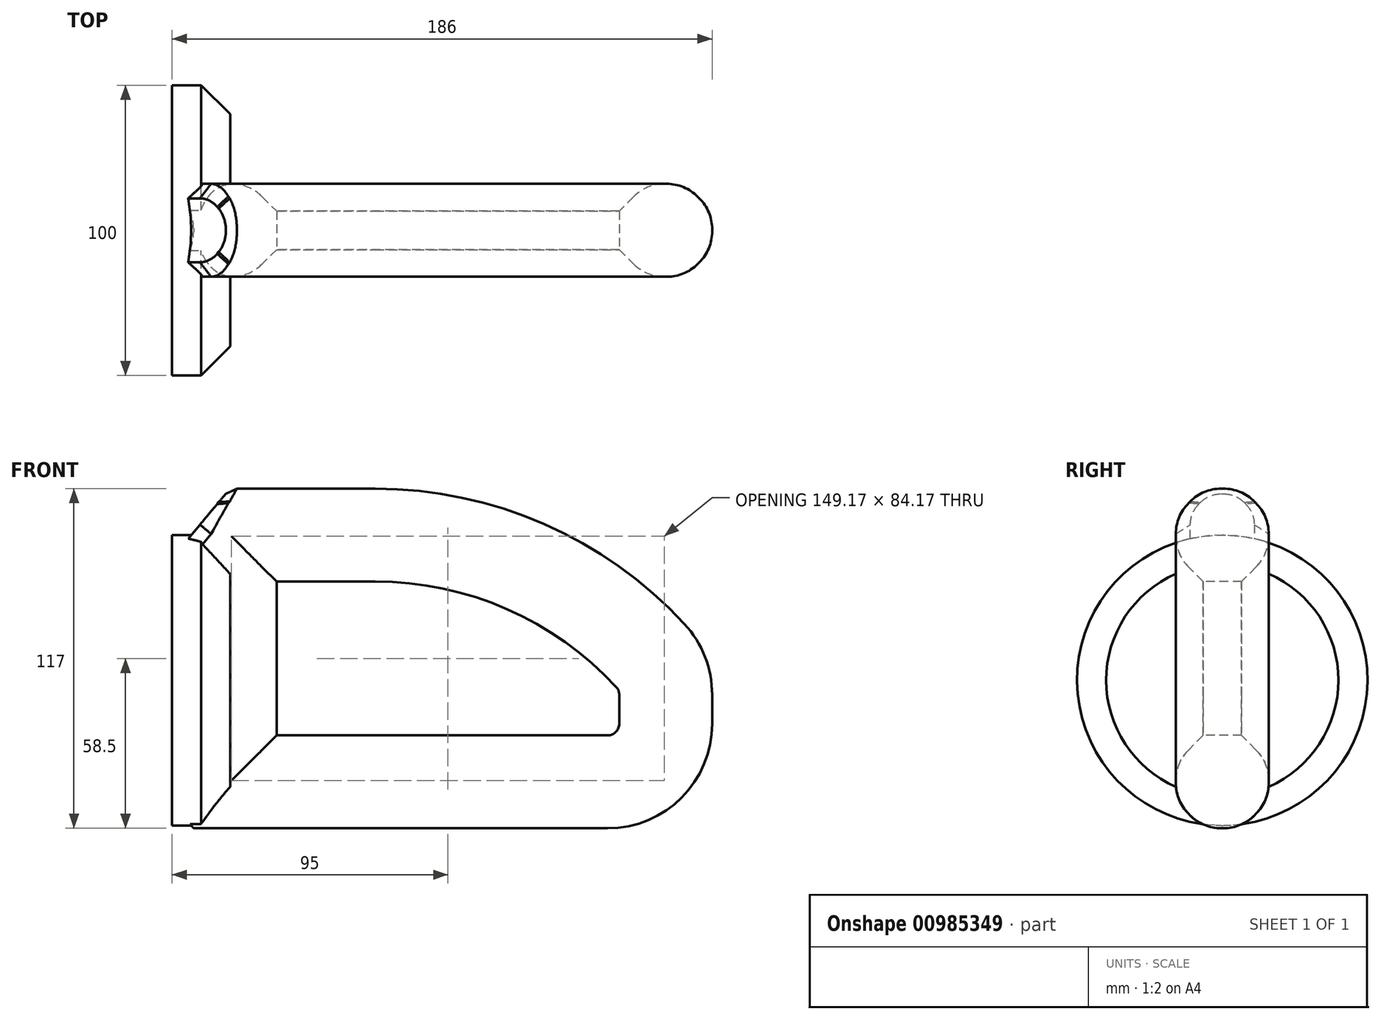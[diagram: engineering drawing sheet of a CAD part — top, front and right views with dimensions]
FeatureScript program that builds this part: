
annotation { "Feature Type Name" : "Feature", "Feature Type Description" : "" }
export const myFeature = defineFeature(function(context is Context, id is Id, definition is map)
    precondition{}
    {
        {
            var Q0;
            Q0=qCreatedBy(makeId("Front.planeOp"),FACE);
            var sketch = newSketch(context, id + "F0", { "sketchPlane" : qUnion([Q0])});
            skLineSegment(sketch, "E0", {"start": v(0, 50) * mm, "end": v(0, -35) * mm});
            skLineSegment(sketch, "E1", {"start": v(0, -35) * mm, "end": v(130, -35) * mm});
            skLineSegment(sketch, "E2", {"start": v(150, -15) * mm, "end": v(150, -5) * mm});
            skLineSegment(sketch, "E3", {"start": v(50, 50) * mm, "end": v(0, 50) * mm});
            skArc(sketch, "E4.filletArc", {"start": v(144.69, 8.57) * mm, "mid": v(101.68, 39.2) * mm, "end": v(50, 50) * mm});
            skArc(sketch, "E5.filletArc", {"start": v(130, -35) * mm, "mid": v(144.14, -29.14) * mm, "end": v(150, -15) * mm});
            skArc(sketch, "E6.filletArc", {"start": v(150, -5) * mm, "mid": v(148.62, 2.29) * mm, "end": v(144.69, 8.57) * mm});
            skSolve(sketch);
        }
        {
            var Q0;
            Q0=qCreatedBy(makeId("Right.planeOp"),FACE);
            var sketch = newSketch(context, id + "F1", { "sketchPlane" : qUnion([Q0])});
            skCircle(sketch, "E7.cCircle", {"center": v(0, 50) * mm, "radius": 16 * mm, "construction": true});
            skLineSegment(sketch, "E7.0", {"start": v(-6.63, 34) * mm, "end": v(-16, 43.37) * mm});
            skLineSegment(sketch, "E7.1", {"start": v(-16, 43.37) * mm, "end": v(-16, 56.63) * mm});
            skLineSegment(sketch, "E7.2", {"start": v(-16, 56.63) * mm, "end": v(-6.63, 66) * mm});
            skLineSegment(sketch, "E7.3", {"start": v(-6.63, 66) * mm, "end": v(6.63, 66) * mm});
            skLineSegment(sketch, "E7.4", {"start": v(6.63, 66) * mm, "end": v(16, 56.63) * mm});
            skLineSegment(sketch, "E7.5", {"start": v(16, 56.63) * mm, "end": v(16, 43.37) * mm});
            skLineSegment(sketch, "E7.6", {"start": v(16, 43.37) * mm, "end": v(6.63, 34) * mm});
            skLineSegment(sketch, "E7.7", {"start": v(6.63, 34) * mm, "end": v(-6.63, 34) * mm});
            skPoint(sketch, "E7.0.midPoint", {"position": v(-11.31, 38.69) * mm});
            skSolve(sketch);
        }
        {
            var Q0;
            Q0=qSketchRegion(id+"F1",true);
            var Q1;
            Q1=qConstructionFilter(qBodyType(qCreatedBy(id+"F0",EDGE),BodyType.WIRE),ConstructionObject.NO);
            sweep(context, id + "F2", {"profiles" : qUnion([Q0]), "path" : qUnion([Q1])});
        }
        {
            var Q0;
            Q0=makeQuery(id+"F2.opSweep","SWEPT_FACE",FACE,{"disambiguationData":[OSD([sQuery(id+"F0.wireOp",EDGE,"E1"),sQuery(id+"F1.wireOp",EDGE,"E7.3")])]});
            var Q1;
            Q1=makeQuery(id+"F2.opSweep","SWEPT_FACE",FACE,{"disambiguationData":[OSD([sQuery(id+"F0.wireOp",EDGE,"E3"),sQuery(id+"F1.wireOp",EDGE,"E7.3")])]});
            var Q2;
            Q2=makeQuery(id+"F2.opSweep","SWEPT_FACE",FACE,{"disambiguationData":[OSD([sQuery(id+"F0.wireOp",EDGE,"E4.filletArc"),sQuery(id+"F1.wireOp",EDGE,"E7.3")])]});
            var Q3;
            Q3=makeQuery(id+"F2.opSweep","SWEPT_FACE",FACE,{"disambiguationData":[OSD([sQuery(id+"F0.wireOp",EDGE,"E6.filletArc"),sQuery(id+"F1.wireOp",EDGE,"E7.3")])]});
            var Q4;
            Q4=makeQuery(id+"F2.opSweep","SWEPT_FACE",FACE,{"disambiguationData":[OSD([sQuery(id+"F0.wireOp",EDGE,"E2"),sQuery(id+"F1.wireOp",EDGE,"E7.3")])]});
            var Q5;
            Q5=makeQuery(id+"F2.opSweep","SWEPT_FACE",FACE,{"disambiguationData":[OSD([sQuery(id+"F0.wireOp",EDGE,"E5.filletArc"),sQuery(id+"F1.wireOp",EDGE,"E7.3")])]});
            var Q6;
            Q6=makeQuery(id+"F2.opSweep","SWEPT_FACE",FACE,{"disambiguationData":[OSD([sQuery(id+"F0.wireOp",EDGE,"E3"),sQuery(id+"F1.wireOp",EDGE,"E7.5")])]});
            var Q7;
            Q7=makeQuery(id+"F2.opSweep","SWEPT_FACE",FACE,{"disambiguationData":[OSD([sQuery(id+"F0.wireOp",EDGE,"E3"),sQuery(id+"F1.wireOp",EDGE,"E7.1")])]});
            fillet(context, id + "F3", {"entities" : qUnion([Q0, Q1, Q2, Q3, Q4, Q5, Q6, Q7]), "radius" : 15 * mm, "tangentPropagation" : true, "allowEdgeOverflow" : false});
        }
        {
            var Q0;
            Q0=qCreatedBy(makeId("Right.planeOp"),FACE);
            var sketch = newSketch(context, id + "F4", { "sketchPlane" : qUnion([Q0])});
            skArc(sketch, "E8.0", {"start": v(16, 50.41) * mm, "mid": v(14.86, 56.15) * mm, "end": v(11.6, 61.02) * mm});
            skLineSegment(sketch, "E8.1", {"start": v(11.02, 61.6) * mm, "end": v(11.6, 61.02) * mm});
            skArc(sketch, "E8.2", {"start": v(0.41, 66) * mm, "mid": v(6.15, 64.86) * mm, "end": v(11.02, 61.6) * mm});
            skLineSegment(sketch, "E8.3", {"start": v(0.41, 66) * mm, "end": v(-0.41, 66) * mm});
            skArc(sketch, "E8.4", {"start": v(-11.02, 61.6) * mm, "mid": v(-6.15, 64.86) * mm, "end": v(-0.41, 66) * mm});
            skLineSegment(sketch, "E8.5", {"start": v(-11.6, 61.02) * mm, "end": v(-11.02, 61.6) * mm});
            skArc(sketch, "E8.6", {"start": v(-11.6, 61.02) * mm, "mid": v(-14.86, 56.15) * mm, "end": v(-16, 50.41) * mm});
            skLineSegment(sketch, "E8.7", {"start": v(16, -35.41) * mm, "end": v(16, 50.41) * mm});
            skLineSegment(sketch, "E8.8", {"start": v(-16, 50.41) * mm, "end": v(-16, -35.41) * mm});
            skArc(sketch, "E9.0", {"start": v(16, -35.41) * mm, "mid": v(14.86, -41.15) * mm, "end": v(11.6, -46.02) * mm});
            skLineSegment(sketch, "E9.1", {"start": v(11.02, -46.6) * mm, "end": v(11.6, -46.02) * mm});
            skArc(sketch, "E9.2", {"start": v(0.41, -51) * mm, "mid": v(6.15, -49.86) * mm, "end": v(11.02, -46.6) * mm});
            skLineSegment(sketch, "E9.3", {"start": v(-0.41, -51) * mm, "end": v(0.41, -51) * mm});
            skArc(sketch, "E9.4", {"start": v(-11.02, -46.6) * mm, "mid": v(-6.15, -49.86) * mm, "end": v(-0.41, -51) * mm});
            skLineSegment(sketch, "E9.5", {"start": v(-11.6, -46.02) * mm, "end": v(-11.02, -46.6) * mm});
            skArc(sketch, "E9.6", {"start": v(-11.6, -46.02) * mm, "mid": v(-14.86, -41.15) * mm, "end": v(-16, -35.41) * mm});
            skSolve(sketch);
        }
        {
            var Q0;
            Q0=qSketchRegion(id+"F4",true);
            var Q1;
            Q1=makeQuery(id+"F2.opSweep","SWEPT_FACE",FACE,{"disambiguationData":[OSD([sQuery(id+"F0.wireOp",EDGE,"E0"),sQuery(id+"F1.wireOp",EDGE,"E7.3")])]});
            extrude(context, id + "F5", {"entities" : qUnion([Q0]), "operationType" : NewBodyOperationType.ADD, "endBound" : BoundingType.UP_TO_SURFACE, "oppositeDirection" : true, "endBoundEntityFace" : qUnion([Q1]), "depth" : 25 * mm});
        }
        {
            var Q0;
            Q0=qCreatedBy(makeId("Front.planeOp"),FACE);
            var sketch = newSketch(context, id + "F6", { "sketchPlane" : qUnion([Q0])});
            skLineSegment(sketch, "E10", {"start": v(0, 66) * mm, "end": v(-16, 46.93) * mm});
            skLineSegment(sketch, "E11", {"start": v(-16, 46.93) * mm, "end": v(-16, 66) * mm});
            skLineSegment(sketch, "E12", {"start": v(-16, 66) * mm, "end": v(0, 66) * mm});
            skLineSegment(sketch, "E13.MirrorCS", {"start": v(-16, -46.93) * mm, "end": v(-16, -66) * mm});
            skLineSegment(sketch, "E14.MirrorCS", {"start": v(-16, -66) * mm, "end": v(0, -66) * mm});
            skLineSegment(sketch, "E15.MirrorCS", {"start": v(0, -66) * mm, "end": v(-16, -46.93) * mm});
            skSolve(sketch);
        }
        {
            var Q0;
            Q0=qSketchRegion(id+"F6",true);
            extrude(context, id + "F7", {"entities" : qUnion([Q0]), "operationType" : NewBodyOperationType.REMOVE, "endBound" : BoundingType.THROUGH_ALL, "oppositeDirection" : true, "depth" : 25 * mm, "hasSecondDirection" : true, "secondDirectionBound" : SecondDirectionBoundingType.THROUGH_ALL, "secondDirectionOppositeDirection" : false, "secondDirectionDepth" : 25 * mm});
        }
        {
            var Q0;
            Q0=qCreatedBy(makeId("Right.planeOp"),FACE);
            var sketch = newSketch(context, id + "F8", { "sketchPlane" : qUnion([Q0])});
            skCircle(sketch, "E16", {"center": v(0, 0) * mm, "radius": 50 * mm});
            skSolve(sketch);
        }
        {
            var Q0;
            Q0=qSketchRegion(id+"F8",true);
            extrude(context, id + "F9", {"entities" : qUnion([Q0]), "operationType" : NewBodyOperationType.ADD, "oppositeDirection" : true, "depth" : 20 * mm});
        }
        {
            var Q0;
            {var subQ0=sQuery(id+"F8.wireOp",EDGE,"E16");Q0=makeQuery(id+"F9.boolean.opBoolean","SPLIT",EDGE,{"disambiguationData":[TD([makeQuery(id+"F5.opExtrude","SWEPT_FACE",FACE,{"disambiguationData":[OSD([sQuery(id+"F4.wireOp",EDGE,"E8.8")])]})])],"derivedFrom":makeQuery(id+"F9.opExtrude","CAP_EDGE",EDGE,{"disambiguationData":[OSD([subQ0])],"isStart":true})});}
            var Q1;
            {var subQ0=sQuery(id+"F8.wireOp",EDGE,"E16");Q1=makeQuery(id+"F9.boolean.opBoolean","SPLIT",EDGE,{"disambiguationData":[TD([makeQuery(id+"F5.opExtrude","SWEPT_FACE",FACE,{"disambiguationData":[OSD([sQuery(id+"F4.wireOp",EDGE,"E8.7")])]})])],"derivedFrom":makeQuery(id+"F9.opExtrude","CAP_EDGE",EDGE,{"disambiguationData":[OSD([subQ0])],"isStart":true})});}
            chamfer(context, id + "F10", {"entities" : qUnion([Q0, Q1]), "width" : 10 * mm, "tangentPropagation" : true});
        }
        {
            var Q0;
            Q0=makeQuery(id+"F7.boolean.opBoolean","INTERSECT",EDGE,{"derivedFrom":[makeQuery(id+"F5.boolean.opBoolean","MERGE",FACE,{"derivedFrom":[makeQuery(id+"F2.opSweep","SWEPT_FACE",FACE,{"disambiguationData":[OSD([sQuery(id+"F0.wireOp",EDGE,"E3"),sQuery(id+"F1.wireOp",EDGE,"E7.1")])]}),makeQuery(id+"F5.opExtrude","SWEPT_FACE",FACE,{"disambiguationData":[OSD([sQuery(id+"F4.wireOp",EDGE,"E8.8")])]})]}),makeQuery(id+"F7.opExtrude","SWEPT_FACE",FACE,{"disambiguationData":[OSD([sQuery(id+"F6.wireOp",EDGE,"E10")])]})]});
            var Q1;
            Q1=makeQuery(id+"F7.boolean.opBoolean","INTERSECT",EDGE,{"derivedFrom":[makeQuery(id+"F5.boolean.opBoolean","MERGE",FACE,{"derivedFrom":[makeQuery(id+"F3.opFillet","BLEND_FACE",FACE,{"disambiguationData":[OSD([sQuery(id+"F0.wireOp",EDGE,"E3"),sQuery(id+"F1.wireOp",EDGE,"E7.1"),sQuery(id+"F1.wireOp",EDGE,"E7.2")])]}),makeQuery(id+"F5.opExtrude","SWEPT_FACE",FACE,{"disambiguationData":[OSD([sQuery(id+"F4.wireOp",EDGE,"E8.6")])]})]}),makeQuery(id+"F7.opExtrude","SWEPT_FACE",FACE,{"disambiguationData":[OSD([sQuery(id+"F6.wireOp",EDGE,"E10")])]})]});
            var Q2;
            Q2=makeQuery(id+"F7.boolean.opBoolean","INTERSECT",EDGE,{"derivedFrom":[makeQuery(id+"F5.boolean.opBoolean","MERGE",FACE,{"derivedFrom":[makeQuery(id+"F2.opSweep","SWEPT_FACE",FACE,{"disambiguationData":[OSD([sQuery(id+"F0.wireOp",EDGE,"E3"),sQuery(id+"F1.wireOp",EDGE,"E7.2")])]}),makeQuery(id+"F5.opExtrude","SWEPT_FACE",FACE,{"disambiguationData":[OSD([sQuery(id+"F4.wireOp",EDGE,"E8.5")])]})]}),makeQuery(id+"F7.opExtrude","SWEPT_FACE",FACE,{"disambiguationData":[OSD([sQuery(id+"F6.wireOp",EDGE,"E10")])]})]});
            var Q3;
            Q3=makeQuery(id+"F7.boolean.opBoolean","INTERSECT",EDGE,{"derivedFrom":[makeQuery(id+"F5.boolean.opBoolean","MERGE",FACE,{"derivedFrom":[makeQuery(id+"F3.opFillet","BLEND_FACE",FACE,{"disambiguationData":[OSD([sQuery(id+"F0.wireOp",EDGE,"E3"),sQuery(id+"F1.wireOp",EDGE,"E7.2"),sQuery(id+"F1.wireOp",EDGE,"E7.3")])]}),makeQuery(id+"F5.opExtrude","SWEPT_FACE",FACE,{"disambiguationData":[OSD([sQuery(id+"F4.wireOp",EDGE,"E8.4")])]})]}),makeQuery(id+"F7.opExtrude","SWEPT_FACE",FACE,{"disambiguationData":[OSD([sQuery(id+"F6.wireOp",EDGE,"E10")])]})]});
            var Q4;
            Q4=makeQuery(id+"F7.boolean.opBoolean","INTERSECT",EDGE,{"derivedFrom":[makeQuery(id+"F5.boolean.opBoolean","MERGE",FACE,{"derivedFrom":[makeQuery(id+"F2.opSweep","SWEPT_FACE",FACE,{"disambiguationData":[OSD([sQuery(id+"F0.wireOp",EDGE,"E3"),sQuery(id+"F1.wireOp",EDGE,"E7.5")])]}),makeQuery(id+"F5.opExtrude","SWEPT_FACE",FACE,{"disambiguationData":[OSD([sQuery(id+"F4.wireOp",EDGE,"E8.7")])]})]}),makeQuery(id+"F7.opExtrude","SWEPT_FACE",FACE,{"disambiguationData":[OSD([sQuery(id+"F6.wireOp",EDGE,"E10")])]})]});
            var Q5;
            Q5=makeQuery(id+"F7.boolean.opBoolean","INTERSECT",EDGE,{"derivedFrom":[makeQuery(id+"F5.boolean.opBoolean","MERGE",FACE,{"derivedFrom":[makeQuery(id+"F3.opFillet","BLEND_FACE",FACE,{"disambiguationData":[OSD([sQuery(id+"F0.wireOp",EDGE,"E3"),sQuery(id+"F1.wireOp",EDGE,"E7.4"),sQuery(id+"F1.wireOp",EDGE,"E7.5")])]}),makeQuery(id+"F5.opExtrude","SWEPT_FACE",FACE,{"disambiguationData":[OSD([sQuery(id+"F4.wireOp",EDGE,"E8.0")])]})]}),makeQuery(id+"F7.opExtrude","SWEPT_FACE",FACE,{"disambiguationData":[OSD([sQuery(id+"F6.wireOp",EDGE,"E10")])]})]});
            var Q6;
            Q6=makeQuery(id+"F7.boolean.opBoolean","INTERSECT",EDGE,{"derivedFrom":[makeQuery(id+"F5.boolean.opBoolean","MERGE",FACE,{"derivedFrom":[makeQuery(id+"F2.opSweep","SWEPT_FACE",FACE,{"disambiguationData":[OSD([sQuery(id+"F0.wireOp",EDGE,"E3"),sQuery(id+"F1.wireOp",EDGE,"E7.4")])]}),makeQuery(id+"F5.opExtrude","SWEPT_FACE",FACE,{"disambiguationData":[OSD([sQuery(id+"F4.wireOp",EDGE,"E8.1")])]})]}),makeQuery(id+"F7.opExtrude","SWEPT_FACE",FACE,{"disambiguationData":[OSD([sQuery(id+"F6.wireOp",EDGE,"E10")])]})]});
            var Q7;
            Q7=makeQuery(id+"F7.boolean.opBoolean","INTERSECT",EDGE,{"derivedFrom":[makeQuery(id+"F5.boolean.opBoolean","MERGE",FACE,{"derivedFrom":[makeQuery(id+"F3.opFillet","BLEND_FACE",FACE,{"disambiguationData":[OSD([sQuery(id+"F0.wireOp",EDGE,"E3"),sQuery(id+"F1.wireOp",EDGE,"E7.3"),sQuery(id+"F1.wireOp",EDGE,"E7.4")])]}),makeQuery(id+"F5.opExtrude","SWEPT_FACE",FACE,{"disambiguationData":[OSD([sQuery(id+"F4.wireOp",EDGE,"E8.2")])]})]}),makeQuery(id+"F7.opExtrude","SWEPT_FACE",FACE,{"disambiguationData":[OSD([sQuery(id+"F6.wireOp",EDGE,"E10")])]})]});
            var Q8;
            Q8=makeQuery(id+"F7.boolean.opBoolean","COPY",EDGE,{"derivedFrom":makeQuery(id+"F7.opExtrude","SWEPT_EDGE",EDGE,{"disambiguationData":[OSD([sQuery(id+"F6.wireOp",EDGE,"E10"),sQuery(id+"F6.wireOp",EDGE,"E12")])]})});
            var Q9;
            Q9=makeQuery(id+"F7.boolean.opBoolean","INTERSECT",EDGE,{"derivedFrom":[makeQuery(id+"F5.boolean.opBoolean","MERGE",FACE,{"derivedFrom":[makeQuery(id+"F2.opSweep","SWEPT_FACE",FACE,{"disambiguationData":[OSD([sQuery(id+"F0.wireOp",EDGE,"E3"),sQuery(id+"F1.wireOp",EDGE,"E7.1")])]}),makeQuery(id+"F5.opExtrude","SWEPT_FACE",FACE,{"disambiguationData":[OSD([sQuery(id+"F4.wireOp",EDGE,"E8.8")])]})]}),makeQuery(id+"F7.opExtrude","SWEPT_FACE",FACE,{"disambiguationData":[OSD([sQuery(id+"F6.wireOp",EDGE,"14d1a042-ea0f-44c2-86e5-6f3f02c37ae91.MirrorCS")])]})]});
            var Q10;
            Q10=makeQuery(id+"F7.boolean.opBoolean","INTERSECT",EDGE,{"derivedFrom":[makeQuery(id+"F5.boolean.opBoolean","MERGE",FACE,{"derivedFrom":[makeQuery(id+"F3.opFillet","BLEND_FACE",FACE,{"disambiguationData":[OSD([sQuery(id+"F0.wireOp",EDGE,"E1"),sQuery(id+"F1.wireOp",EDGE,"E7.1"),sQuery(id+"F1.wireOp",EDGE,"E7.2")])]}),makeQuery(id+"F5.opExtrude","SWEPT_FACE",FACE,{"disambiguationData":[OSD([sQuery(id+"F4.wireOp",EDGE,"E8.9")])]})]}),makeQuery(id+"F7.opExtrude","SWEPT_FACE",FACE,{"disambiguationData":[OSD([sQuery(id+"F6.wireOp",EDGE,"14d1a042-ea0f-44c2-86e5-6f3f02c37ae91.MirrorCS")])]})]});
            chamfer(context, id + "F11", {"entities" : qUnion([Q0, Q1, Q2, Q3, Q4, Q5, Q6, Q7, Q8, Q9, Q10]), "width" : 5 * mm, "tangentPropagation" : true});
        }
    });
